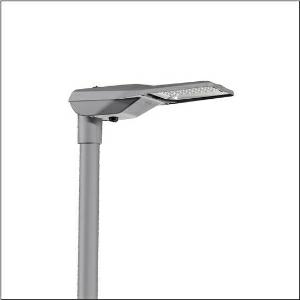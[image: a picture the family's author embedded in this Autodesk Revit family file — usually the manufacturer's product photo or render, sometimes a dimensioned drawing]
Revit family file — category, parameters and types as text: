
# Revit family: streetlight_sl_21_mini___st1_0a_5xe2d33t08hb_cfc2
name_source: partatom
category: Lighting Fixtures
units: mm (PartAtom-declared; Revit-internal decimal feet)

## family parameters
Cut with Voids When Loaded = No
Host = Face
Light Source = No
Part Type = Normal
Room Calculation Point = No
Round Connector Dimension = Use Diameter
Shared = No

## types (1)
- --- (1 x LED, 9040 lm, 66 W, 3000K)
    Apparent Load = 66 VA
    CIE Flux Codes = 37 72 97 100 100
    Color Rendering = 70
    Color Temperature = 3000K
    Default Elevation = 1800 mm
    Description = Streetlight SL 21 mini, mast luminaire, primary light control with lens, of PMMA, primary optical cover: cover, of toughened safety glass, transparent, light distribution: ST1.0a, light emission: direct distribution, primary light characteristic: asymmetric, installation type: side-entry, post-top, LED, High Power LED, rated luminous flux: 9.040lm, luminous efficacy: 137lm/W, light colour: 730, colour temperature: 3000K, control gear: D4i, control: flexible luminous flux parameterisation, time-dependent luminous flux control, constant luminous flux control, overheat protection, pre-setting: logarithmic dimming characteristic, mains connection: 220..240V, AC, 50/60Hz, start of lifetime: 66W, end of service life: 69W, reduction: 30W, luminaire housing, of diecast aluminium, powder-coated, SITECO metallic grey (DB 702S), corrosivity category C5 high according to DIN EN ISO 12944, please order mast flange separately, inclination adjustable: 0°, 5°, 10°, 15°, sealing non-destructively replaceable, multi-level sealing system, length: 628mm, width: 235mm, height: 110mm, mast flange for spigot size: 42mm (side-entry): 5XC10008XM4, 60/48mm (side-entry/post-top): 5XC10108XM2, 76/60mm (side-entry/post-top): 5XC10108XM1, mounting height: 4..8m, Smart Interface below and above, protection rating (complete): IP66, insulation class (complete): insulation class II (safety insulation), certification: CE, ENEC, ENEC+, VDE, impact resistance: IK10, permissible operating ambient temperature for outdoor applications: -40..+50°C, standard-compliant lighting for roads and squares, packaging unit: 1 piece

Light Distribution: ST1.0a
    Height = 110 mm
    Lamp = 1 x LED
    Lamp Light Flux = 9040 lm
    Lamp Power = 66 W
    Lamp count = 1
    Length = 625 mm
    Luminous efficacy = 137 lm/W
    Manufacturer = Siteco
    ModVariant = No
    Model = 5XE2D33T08HB
    Number of Poles = 1
    OnlyDefault = Yes
    Power Factor = 1
    Product Name = Streetlight SL 21 mini | ST1.0a
    Product group = mast luminaire | pylon top
    ProductGroupID = 6100
    Protection Class = Protection class II
    Protection Degree = IP 66
    RLX_Detail_Level = 1
    RLX_Emergency_Light_Flux = 0 lm
    RLX_Emergency_Type = 0
    RLX_Emergency_Type_DB = No
    RlxData = <blob elided: 26317 chars, md5=75a6ae60>
    Socket = socket
    Standby Power = 0 W
    System Light Flux = 9040 lm
    System Power = 66 W
    Type Comments = factory setting: luminous flux: 100 % | dim-lin: 254 | 670 mA
    Type Image = l_1003514.jpg
    URL = http://relux.com
    VarID = @adj_185935
    Voltage = 0 V
    Weight = 0.00 kg
    Width = 234 mm

## geometry (parser evidence)
native form markers: Blend x4, Sweep x10
no freeform markers — native parametric forms only
